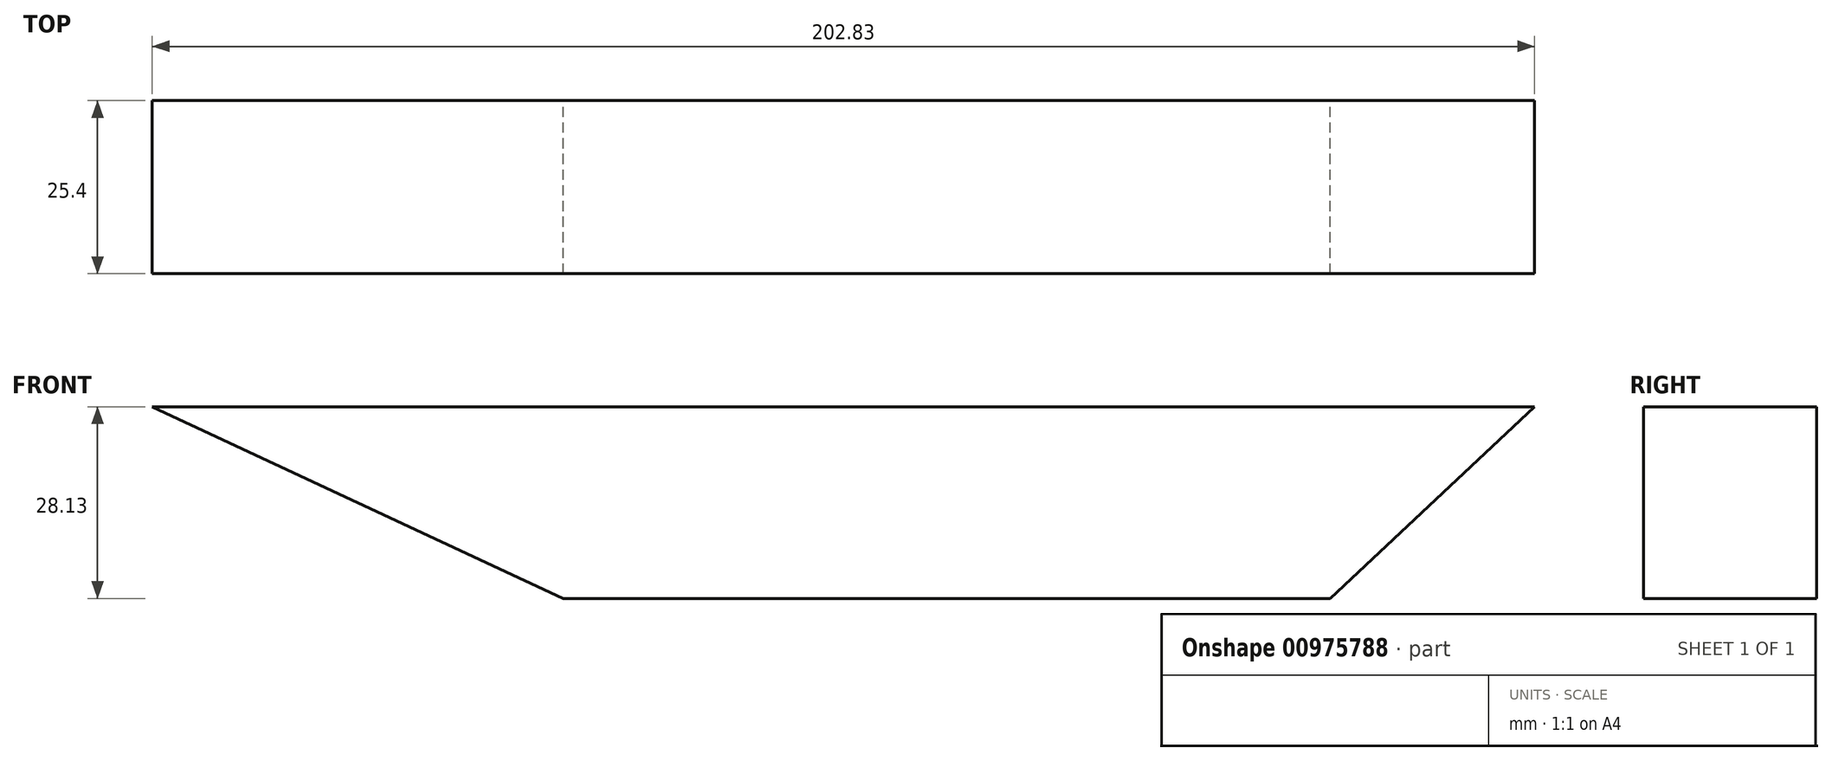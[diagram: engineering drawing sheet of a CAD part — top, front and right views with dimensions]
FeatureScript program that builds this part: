
annotation { "Feature Type Name" : "Feature", "Feature Type Description" : "" }
export const myFeature = defineFeature(function(context is Context, id is Id, definition is map)
    precondition{}
    {
        {
            var Q0;
            Q0=qCreatedBy(makeId("Front.planeOp"),FACE);
            var sketch = newSketch(context, id + "F0", { "sketchPlane" : qUnion([Q0])});
            skLineSegment(sketch, "E0.bottom", {"start": v(-53.91, 21.72) * mm, "end": v(58.6, 21.72) * mm});
            skLineSegment(sketch, "E0.top", {"start": v(-53.91, -6.4) * mm, "end": v(58.6, -6.4) * mm});
            skLineSegment(sketch, "E0.left", {"start": v(-53.91, 21.72) * mm, "end": v(-53.91, -6.4) * mm});
            skLineSegment(sketch, "E0.right", {"start": v(58.6, 21.72) * mm, "end": v(58.6, -6.4) * mm});
            skLineSegment(sketch, "E1", {"start": v(-53.91, 21.72) * mm, "end": v(-114.23, 21.72) * mm});
            skLineSegment(sketch, "E2", {"start": v(-114.23, 21.72) * mm, "end": v(-53.91, -6.4) * mm});
            skLineSegment(sketch, "E3", {"start": v(58.6, 21.72) * mm, "end": v(88.6, 21.72) * mm});
            skLineSegment(sketch, "E4", {"start": v(58.6, -6.4) * mm, "end": v(88.6, 21.72) * mm});
            skSolve(sketch);
        }
        {
            var Q0;
            Q0=makeQuery(id+"F0.imprint","IMPRINT",FACE,{"disambiguationData":[TD([[makeQuery(id+"F0.imprint","IMPRINT",EDGE,{"derivedFrom":sQuery(id+"F0.wireOp",EDGE,"E0.bottom")}),-1.0]])]});
            extrude(context, id + "F1", {"entities" : qUnion([Q0]), "depth" : 25.4 * mm, "offsetDistance" : 25.4 * mm});
        }
        {
            var Q0;
            Q0 = qSketchRegion(id + "F0", true);
            extrude(context, id + "F2", {"entities" : qUnion([Q0]), "operationType" : NewBodyOperationType.ADD, "depth" : 25.4 * mm, "offsetDistance" : 25.4 * mm});
        }
    });
